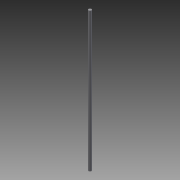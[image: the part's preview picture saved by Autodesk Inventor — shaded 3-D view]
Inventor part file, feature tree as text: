
AUTODESK INVENTOR PART (.ipt)
format: ipt  version: 2013 SP2 (Build 170200200, 200)  size: 60,928 bytes
history: native  units: mm
features: extrude x1, sketch x1
ambient origin geometry x8: Origin, YZ Plane, XZ Plane, XY Plane, X Axis, Y Axis, Z Axis, Center Point
bodies: Solid1 (feature_tree)
feature tree (2):
  extrude  "Extrusion1"  Depth=400.0mm TaperAngle=0.0deg
  sketch  "Sketch1"  dims[d0=8.0mm d1=400.0mm d2=0.0mm]
